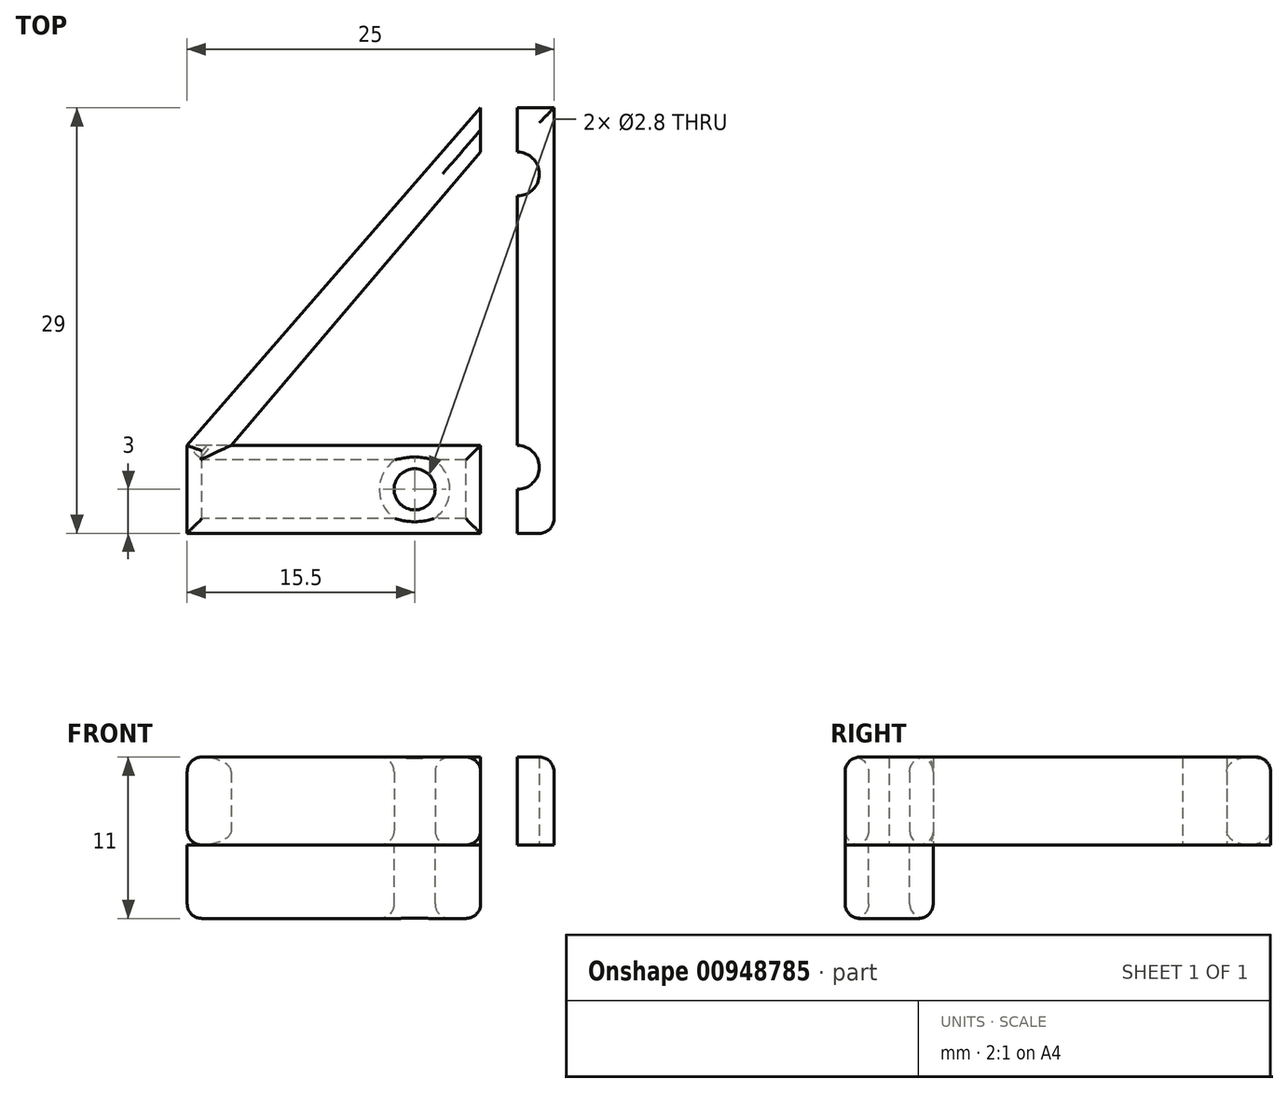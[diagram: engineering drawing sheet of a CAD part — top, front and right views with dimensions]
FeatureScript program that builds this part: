
annotation { "Feature Type Name" : "Feature", "Feature Type Description" : "" }
export const myFeature = defineFeature(function(context is Context, id is Id, definition is map)
    precondition{}
    {
        {
            var Q0;
            Q0=qCreatedBy(makeId("Top.planeOp"),FACE);
            var sketch = newSketch(context, id + "F0", { "sketchPlane" : qUnion([Q0])});
            skLineSegment(sketch, "E0.bottom", {"start": v(0, 0) * mm, "end": v(-20, 0) * mm});
            skLineSegment(sketch, "E0.top", {"start": v(0, 6) * mm, "end": v(-20, 6) * mm});
            skLineSegment(sketch, "E0.left", {"start": v(0, 0) * mm, "end": v(0, 6) * mm});
            skLineSegment(sketch, "E0.right", {"start": v(-20, 0) * mm, "end": v(-20, 6) * mm});
            skLineSegment(sketch, "E1", {"start": v(-20, 3) * mm, "end": v(0, 3) * mm});
            skCircle(sketch, "E2", {"center": v(-15.5, 3) * mm, "radius": 1.4 * mm});
            skCircle(sketch, "E3", {"center": v(-4.5, 3) * mm, "radius": 1.4 * mm});
            skPoint(sketch, "E4", {"position": v(-15.5, 4.4) * mm});
            skPoint(sketch, "E5", {"position": v(-4.5, 4.4) * mm});
            skPoint(sketch, "E6", {"position": v(-4.5, 1.6) * mm});
            skPoint(sketch, "E7", {"position": v(-15.5, 1.6) * mm});
            skLineSegment(sketch, "E8", {"start": v(-15.5, 4.4) * mm, "end": v(-4.5, 4.4) * mm});
            skLineSegment(sketch, "E9", {"start": v(-4.5, 1.6) * mm, "end": v(-15.5, 1.6) * mm});
            skLineSegment(sketch, "E10.bottom", {"start": v(0, 0) * mm, "end": v(5, 0) * mm});
            skLineSegment(sketch, "E10.top", {"start": v(0, 29) * mm, "end": v(5, 29) * mm});
            skLineSegment(sketch, "E10.left", {"start": v(0, 0) * mm, "end": v(0, 29) * mm});
            skLineSegment(sketch, "E10.right", {"start": v(5, 0) * mm, "end": v(5, 29) * mm});
            skPoint(sketch, "E11", {"position": v(5, 15) * mm});
            skLineSegment(sketch, "E12", {"start": v(5, 15) * mm, "end": v(5, 29) * mm});
            skLineSegment(sketch, "E13", {"start": v(2.5, 29) * mm, "end": v(2.5, 0) * mm});
            skCircle(sketch, "E14", {"center": v(2.5, 24.5) * mm, "radius": 1.5 * mm});
            skCircle(sketch, "E15", {"center": v(2.5, 4.5) * mm, "radius": 1.5 * mm});
            skPoint(sketch, "E16", {"position": v(0, 26) * mm});
            skPoint(sketch, "E17", {"position": v(-17, 6) * mm});
            skLineSegment(sketch, "E18", {"start": v(0, 29) * mm, "end": v(-20, 6) * mm});
            skLineSegment(sketch, "E19", {"start": v(-17, 6) * mm, "end": v(0, 26) * mm});
            skLineSegment(sketch, "E20.bottom", {"start": v(-11.5, 4.4) * mm, "end": v(-8.5, 4.4) * mm});
            skLineSegment(sketch, "E20.top", {"start": v(-11.5, 1.6) * mm, "end": v(-8.5, 1.6) * mm});
            skLineSegment(sketch, "E20.left", {"start": v(-11.5, 4.4) * mm, "end": v(-11.5, 1.6) * mm});
            skLineSegment(sketch, "E20.right", {"start": v(-8.5, 4.4) * mm, "end": v(-8.5, 1.6) * mm});
            skLineSegment(sketch, "E21", {"start": v(-10, 4.4) * mm, "end": v(-10, 1.6) * mm});
            skSolve(sketch);
        }
        {
            var Q0;
            {var subQ0=sQuery(id+"F0.wireOp",EDGE,"E18");Q0=makeQuery(id+"F0.imprint","IMPRINT",FACE,{"disambiguationData":[TD([[makeQuery(id+"F0.imprint","IMPRINT",EDGE,{"derivedFrom":subQ0}),1.0]])]});}
            var Q1;
            {var subQ11=sQuery(id+"F0.wireOp",EDGE,"E10.left");var subQ14=makeQuery(id+"F0.imprint","INTERSECT",VERTEX,{"derivedFrom":[sQuery(id+"F0.wireOp",EDGE,"E0.top"),subQ11]});Q1=makeQuery(id+"F0.imprint","IMPRINT",FACE,{"disambiguationData":[TD([[makeQuery(id+"F0.imprint","IMPRINT",EDGE,{"disambiguationData":[TD([[subQ14,1.0]])],"derivedFrom":subQ11}),-1.0]])]});}
            var Q2;
            {var subQ1=sQuery(id+"F0.wireOp",EDGE,"E10.right");Q2=makeQuery(id+"F0.imprint","IMPRINT",FACE,{"disambiguationData":[TD([[makeQuery(id+"F0.imprint","IMPRINT",EDGE,{"derivedFrom":subQ1}),1.0]])]});}
            var Q3;
            {var subQ13=sQuery(id+"F0.wireOp",EDGE,"E8");Q3=makeQuery(id+"F0.imprint","IMPRINT",FACE,{"disambiguationData":[TD([[makeQuery(id+"F0.imprint","IMPRINT",EDGE,{"derivedFrom":subQ13}),1.0]])]});}
            var Q4;
            {var subQ6=sQuery(id+"F0.wireOp",EDGE,"E0.bottom");Q4=makeQuery(id+"F0.imprint","IMPRINT",FACE,{"disambiguationData":[TD([[makeQuery(id+"F0.imprint","IMPRINT",EDGE,{"derivedFrom":subQ6}),-1.0]])]});}
            extrude(context, id + "F1", {"entities" : qUnion([Q0, Q1, Q2, Q3, Q4]), "depth" : 6 * mm, "offsetDistance" : 25 * mm});
        }
        {
            var Q0;
            {var subQ0=sQuery(id+"F0.wireOp",EDGE,"E2");var subQ1=sQuery(id+"F0.wireOp",EDGE,"E1");var subQ2=makeQuery(id+"F0.imprint","INTERSECT",VERTEX,{"disambiguationData":[OD(0.0)],"derivedFrom":[subQ1,subQ0]});Q0=makeQuery(id+"F0.imprint","IMPRINT",FACE,{"disambiguationData":[TD([[makeQuery(id+"F0.imprint","IMPRINT",EDGE,{"disambiguationData":[TD([[subQ2,-1.0]])],"derivedFrom":subQ1}),-1.0]])]});}
            var Q1;
            {var subQ5=sQuery(id+"F0.wireOp",EDGE,"E9");Q1=makeQuery(id+"F0.imprint","IMPRINT",FACE,{"disambiguationData":[TD([[makeQuery(id+"F0.imprint","IMPRINT",EDGE,{"derivedFrom":subQ5}),-1.0]])]});}
            var Q2;
            {var subQ5=sQuery(id+"F0.wireOp",EDGE,"E8");Q2=makeQuery(id+"F0.imprint","IMPRINT",FACE,{"disambiguationData":[TD([[makeQuery(id+"F0.imprint","IMPRINT",EDGE,{"derivedFrom":subQ5}),-1.0]])]});}
            var Q3;
            {var subQ0=sQuery(id+"F0.wireOp",EDGE,"E3");var subQ1=sQuery(id+"F0.wireOp",EDGE,"E1");var subQ2=makeQuery(id+"F0.imprint","INTERSECT",VERTEX,{"disambiguationData":[OD(0.0)],"derivedFrom":[subQ1,subQ0]});Q3=makeQuery(id+"F0.imprint","IMPRINT",FACE,{"disambiguationData":[TD([[makeQuery(id+"F0.imprint","IMPRINT",EDGE,{"disambiguationData":[TD([[subQ2,-1.0]])],"derivedFrom":subQ1}),1.0]])]});}
            var Q4;
            {var subQ0=sQuery(id+"F0.wireOp",EDGE,"E3");var subQ1=sQuery(id+"F0.wireOp",EDGE,"E1");var subQ2=makeQuery(id+"F0.imprint","INTERSECT",VERTEX,{"disambiguationData":[OD(0.0)],"derivedFrom":[subQ1,subQ0]});Q4=makeQuery(id+"F0.imprint","IMPRINT",FACE,{"disambiguationData":[TD([[makeQuery(id+"F0.imprint","IMPRINT",EDGE,{"disambiguationData":[TD([[subQ2,-1.0]])],"derivedFrom":subQ1}),-1.0]])]});}
            var Q5;
            {var subQ0=sQuery(id+"F0.wireOp",EDGE,"E2");var subQ1=sQuery(id+"F0.wireOp",EDGE,"E1");var subQ2=makeQuery(id+"F0.imprint","INTERSECT",VERTEX,{"disambiguationData":[OD(0.0)],"derivedFrom":[subQ1,subQ0]});Q5=makeQuery(id+"F0.imprint","IMPRINT",FACE,{"disambiguationData":[TD([[makeQuery(id+"F0.imprint","IMPRINT",EDGE,{"disambiguationData":[TD([[subQ2,-1.0]])],"derivedFrom":subQ1}),1.0]])]});}
            extrude(context, id + "F2", {"entities" : qUnion([Q0, Q1, Q2, Q3, Q4, Q5]), "operationType" : NewBodyOperationType.ADD, "depth" : 6 * mm, "offsetDistance" : 25 * mm});
        }
        {
            var Q0;
            Q0=makeQuery(id+"F2.opExtrude","CAP_FACE",FACE,{"disambiguationData":[OSD([sQuery(id+"F0.wireOp",EDGE,"E2"),sQuery(id+"F0.wireOp",EDGE,"E3"),sQuery(id+"F0.wireOp",EDGE,"E8"),sQuery(id+"F0.wireOp",EDGE,"E9")])],"isStart":false});
            fillet(context, id + "F3", {"entities" : qUnion([Q0]), "radius" : 1 * mm, "tangentPropagation" : true, "allowEdgeOverflow" : false});
        }
        {
            var Q0;
            {var subQ0=sQuery(id+"F0.wireOp",EDGE,"E9");var subQ1=sQuery(id+"F0.wireOp",EDGE,"E8");var subQ2=sQuery(id+"F0.wireOp",EDGE,"E3");var subQ3=sQuery(id+"F0.wireOp",EDGE,"E2");Q0=makeQuery(id+"F2.boolean.opBoolean","MERGE",FACE,{"derivedFrom":[makeQuery(id+"F1.opExtrude","CAP_FACE",FACE,{"disambiguationData":[OSD([sQuery(id+"F0.wireOp",EDGE,"E0.bottom"),sQuery(id+"F0.wireOp",EDGE,"E0.top"),sQuery(id+"F0.wireOp",EDGE,"E0.right"),subQ3,subQ2,subQ1,subQ0,sQuery(id+"F0.wireOp",EDGE,"E10.bottom"),sQuery(id+"F0.wireOp",EDGE,"E10.top"),sQuery(id+"F0.wireOp",EDGE,"E10.left"),sQuery(id+"F0.wireOp",EDGE,"E10.right"),sQuery(id+"F0.wireOp",EDGE,"E12"),sQuery(id+"F0.wireOp",EDGE,"E14"),sQuery(id+"F0.wireOp",EDGE,"E15"),sQuery(id+"F0.wireOp",EDGE,"E18"),sQuery(id+"F0.wireOp",EDGE,"E19")])],"isStart":true}),makeQuery(id+"F2.opExtrude","CAP_FACE",FACE,{"disambiguationData":[OSD([subQ3,subQ2,subQ1,subQ0])],"isStart":true})]});}
            var Q1;
            Q1=makeQuery(id+"F1.opExtrude","CAP_EDGE",EDGE,{"disambiguationData":[OSD([sQuery(id+"F0.wireOp",EDGE,"E10.right"),sQuery(id+"F0.wireOp",EDGE,"E12")])],"isStart":false});
            var Q2;
            Q2=makeQuery(id+"F1.opExtrude","SWEPT_EDGE",EDGE,{"disambiguationData":[OSD([sQuery(id+"F0.wireOp",EDGE,"E10.bottom"),sQuery(id+"F0.wireOp",EDGE,"E10.right")])]});
            var Q3;
            Q3=makeQuery(id+"F1.opExtrude","CAP_EDGE",EDGE,{"disambiguationData":[OSD([sQuery(id+"F0.wireOp",EDGE,"E18")])],"isStart":false});
            var Q4;
            Q4=makeQuery(id+"F1.opExtrude","CAP_EDGE",EDGE,{"disambiguationData":[OSD([sQuery(id+"F0.wireOp",EDGE,"E0.right")])],"isStart":false});
            var Q5;
            Q5=makeQuery(id+"F1.opExtrude","CAP_EDGE",EDGE,{"disambiguationData":[OSD([sQuery(id+"F0.wireOp",EDGE,"E10.top")])],"isStart":false});
            var Q6;
            Q6=makeQuery(id+"F1.opExtrude","CAP_EDGE",EDGE,{"disambiguationData":[OSD([sQuery(id+"F0.wireOp",EDGE,"E0.bottom"),sQuery(id+"F0.wireOp",EDGE,"E10.bottom")])],"isStart":false});
            fillet(context, id + "F4", {"entities" : qUnion([Q0, Q1, Q2, Q3, Q4, Q5, Q6]), "radius" : 1 * mm, "tangentPropagation" : true, "allowEdgeOverflow" : false});
        }
        {
            var Q0;
            {var subQ0=sQuery(id+"F0.wireOp",EDGE,"E2");var subQ1=sQuery(id+"F0.wireOp",EDGE,"E1");var subQ2=makeQuery(id+"F0.imprint","INTERSECT",VERTEX,{"disambiguationData":[OD(0.0)],"derivedFrom":[subQ1,subQ0]});Q0=makeQuery(id+"F0.imprint","IMPRINT",FACE,{"disambiguationData":[TD([[makeQuery(id+"F0.imprint","IMPRINT",EDGE,{"disambiguationData":[TD([[subQ2,-1.0]])],"derivedFrom":subQ1}),-1.0]])]});}
            var Q1;
            {var subQ0=sQuery(id+"F0.wireOp",EDGE,"E2");var subQ1=sQuery(id+"F0.wireOp",EDGE,"E1");var subQ2=makeQuery(id+"F0.imprint","INTERSECT",VERTEX,{"disambiguationData":[OD(0.0)],"derivedFrom":[subQ1,subQ0]});Q1=makeQuery(id+"F0.imprint","IMPRINT",FACE,{"disambiguationData":[TD([[makeQuery(id+"F0.imprint","IMPRINT",EDGE,{"disambiguationData":[TD([[subQ2,-1.0]])],"derivedFrom":subQ1}),1.0]])]});}
            var Q2;
            {var subQ5=sQuery(id+"F0.wireOp",EDGE,"E8");Q2=makeQuery(id+"F0.imprint","IMPRINT",FACE,{"disambiguationData":[TD([[makeQuery(id+"F0.imprint","IMPRINT",EDGE,{"derivedFrom":subQ5}),-1.0]])]});}
            var Q3;
            {var subQ5=sQuery(id+"F0.wireOp",EDGE,"E9");Q3=makeQuery(id+"F0.imprint","IMPRINT",FACE,{"disambiguationData":[TD([[makeQuery(id+"F0.imprint","IMPRINT",EDGE,{"derivedFrom":subQ5}),-1.0]])]});}
            var Q4;
            {var subQ0=sQuery(id+"F0.wireOp",EDGE,"E3");var subQ1=sQuery(id+"F0.wireOp",EDGE,"E1");var subQ2=makeQuery(id+"F0.imprint","INTERSECT",VERTEX,{"disambiguationData":[OD(0.0)],"derivedFrom":[subQ1,subQ0]});Q4=makeQuery(id+"F0.imprint","IMPRINT",FACE,{"disambiguationData":[TD([[makeQuery(id+"F0.imprint","IMPRINT",EDGE,{"disambiguationData":[TD([[subQ2,-1.0]])],"derivedFrom":subQ1}),-1.0]])]});}
            var Q5;
            {var subQ0=sQuery(id+"F0.wireOp",EDGE,"E3");var subQ1=sQuery(id+"F0.wireOp",EDGE,"E1");var subQ2=makeQuery(id+"F0.imprint","INTERSECT",VERTEX,{"disambiguationData":[OD(0.0)],"derivedFrom":[subQ1,subQ0]});Q5=makeQuery(id+"F0.imprint","IMPRINT",FACE,{"disambiguationData":[TD([[makeQuery(id+"F0.imprint","IMPRINT",EDGE,{"disambiguationData":[TD([[subQ2,-1.0]])],"derivedFrom":subQ1}),1.0]])]});}
            extrude(context, id + "F5", {"entities" : qUnion([Q0, Q1, Q2, Q3, Q4, Q5]), "operationType" : NewBodyOperationType.ADD, "oppositeDirection" : true, "depth" : 5 * mm, "offsetDistance" : 25 * mm});
        }
        {
            var Q0;
            Q0=makeQuery(id+"F5.opExtrude","CAP_FACE",FACE,{"disambiguationData":[OSD([sQuery(id+"F0.wireOp",EDGE,"E2"),sQuery(id+"F0.wireOp",EDGE,"E3"),sQuery(id+"F0.wireOp",EDGE,"E8"),sQuery(id+"F0.wireOp",EDGE,"E9")])],"isStart":false});
            fillet(context, id + "F6", {"entities" : qUnion([Q0]), "radius" : 1 * mm, "tangentPropagation" : true, "allowEdgeOverflow" : false});
        }
    });
